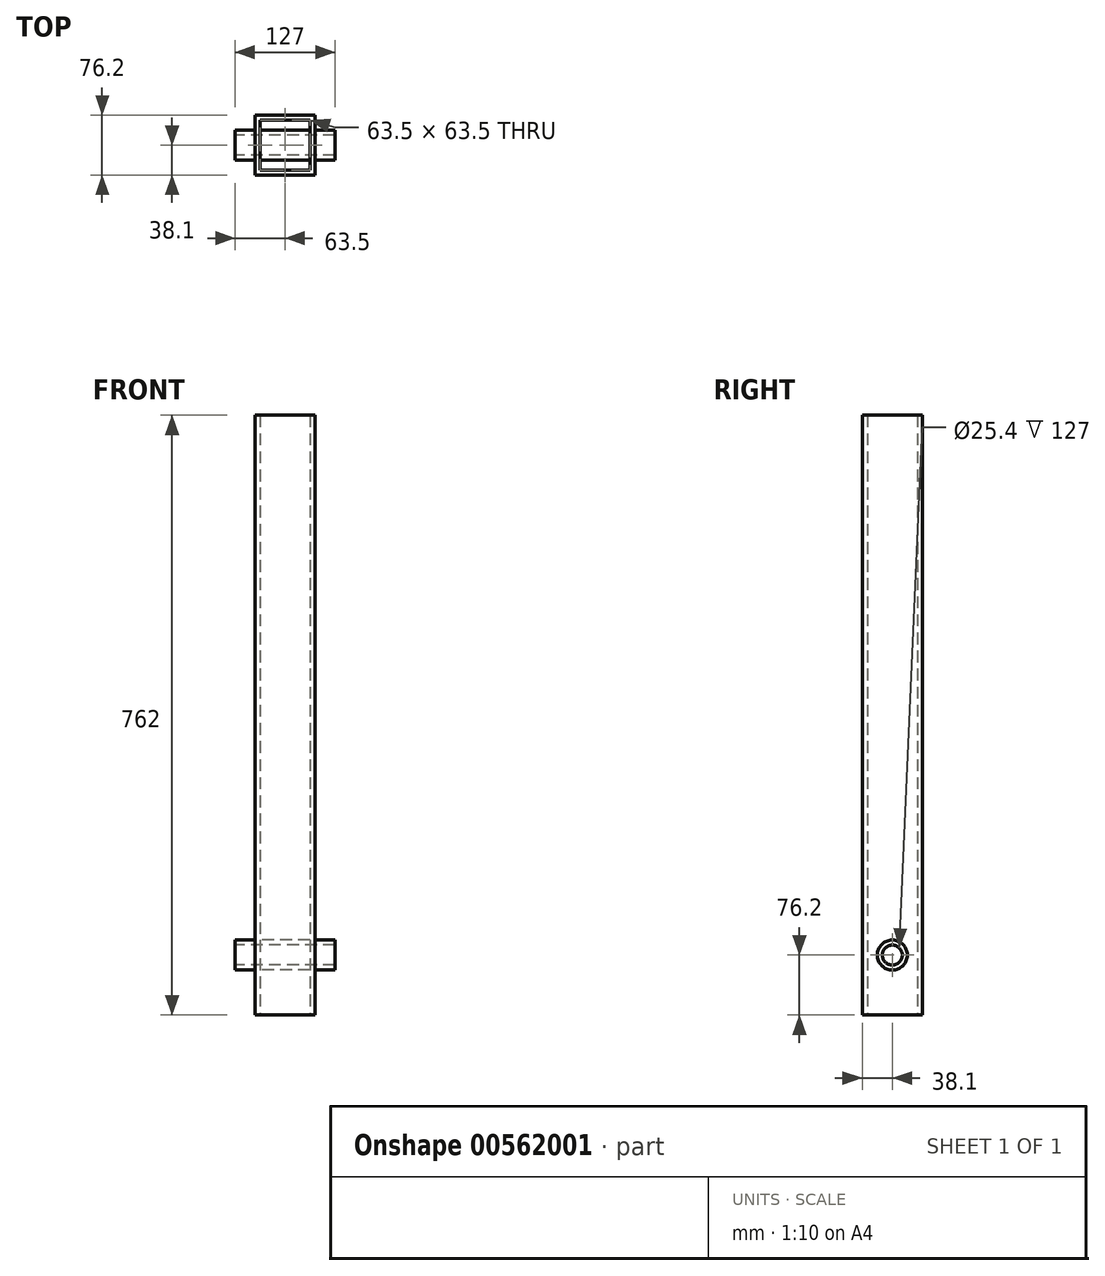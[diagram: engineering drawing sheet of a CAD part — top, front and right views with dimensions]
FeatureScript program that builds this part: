
annotation { "Feature Type Name" : "Feature", "Feature Type Description" : "" }
export const myFeature = defineFeature(function(context is Context, id is Id, definition is map)
    precondition{}
    {
        {
            var Q0;
            Q0=qCreatedBy(makeId("Top.planeOp"),FACE);
            var sketch = newSketch(context, id + "F0", { "sketchPlane" : qUnion([Q0])});
            skLineSegment(sketch, "E0.bottom", {"start": v(38.1, -38.1) * mm, "end": v(-38.1, -38.1) * mm});
            skLineSegment(sketch, "E0.top", {"start": v(38.1, 38.1) * mm, "end": v(-38.1, 38.1) * mm});
            skLineSegment(sketch, "E0.left", {"start": v(38.1, -38.1) * mm, "end": v(38.1, 38.1) * mm});
            skLineSegment(sketch, "E0.right", {"start": v(-38.1, -38.1) * mm, "end": v(-38.1, 38.1) * mm});
            skPoint(sketch, "E0.middle", {"position": v(0, 0) * mm});
            skLineSegment(sketch, "E1.bottom", {"start": v(31.75, -31.75) * mm, "end": v(-31.75, -31.75) * mm});
            skLineSegment(sketch, "E1.top", {"start": v(31.75, 31.75) * mm, "end": v(-31.75, 31.75) * mm});
            skLineSegment(sketch, "E1.left", {"start": v(31.75, -31.75) * mm, "end": v(31.75, 31.75) * mm});
            skLineSegment(sketch, "E1.right", {"start": v(-31.75, -31.75) * mm, "end": v(-31.75, 31.75) * mm});
            skLineSegment(sketch, "E2", {"start": v(0, 0) * mm, "end": v(38.1, -38.1) * mm, "construction": true});
            skSolve(sketch);
        }
        {
            var Q0;
            Q0 = qSketchRegion(id + "F0", true);
            extrude(context, id + "F1", {"entities" : qUnion([Q0]), "depth" : 762 * mm, "offsetDistance" : 25.4 * mm});
        }
        {
            var Q0;
            Q0=makeQuery(id+"F1.opExtrude","SWEPT_FACE",FACE,{"disambiguationData":[OSD([sQuery(id+"F0.wireOp",EDGE,"E0.left")])]});
            var sketch = newSketch(context, id + "F2", { "sketchPlane" : qUnion([Q0])});
            skCircle(sketch, "E3", {"center": v(0, 76.2) * mm, "radius": 19.05 * mm});
            skSolve(sketch);
        }
        {
            var Q0;
            Q0 = qSketchRegion(id + "F2", true);
            extrude(context, id + "F3", {"entities" : qUnion([Q0]), "operationType" : NewBodyOperationType.ADD, "depth" : 25.4 * mm, "offsetDistance" : 25.4 * mm, "hasSecondDirection" : true, "secondDirectionOppositeDirection" : true, "secondDirectionDepth" : 101.6 * mm});
        }
        {
            var Q0;
            Q0=makeQuery(id+"F3.opExtrude","CAP_FACE",FACE,{"disambiguationData":[OSD([sQuery(id+"F2.wireOp",EDGE,"E3")])],"isStart":true});
            var sketch = newSketch(context, id + "F4", { "sketchPlane" : qUnion([Q0])});
            skCircle(sketch, "E4", {"center": v(0, 76.2) * mm, "radius": 12.7 * mm});
            skSolve(sketch);
        }
        {
            var Q0;
            Q0 = qSketchRegion(id + "F4", true);
            extrude(context, id + "F5", {"entities" : qUnion([Q0]), "operationType" : NewBodyOperationType.REMOVE, "endBound" : BoundingType.THROUGH_ALL, "oppositeDirection" : true, "depth" : 25.4 * mm, "offsetDistance" : 25.4 * mm});
        }
    });
